# Revit family: MH-205-G
name_source: partatom
category: Plumbing Fixtures
revit_build: Autodesk Revit 2015 (Build: 20140322_1515(x64)
units: mm (PartAtom-declared; Revit-internal decimal feet)

## types (2) — shared parameters
A = 13"
A' = 6 1/2"
B = 11 25/32"
B' = 5 7/8"
B01 = 5 1/2"
C = 7 9/32"
C' = 3 21/32"
C'1 = 4 1/16"
Default Elevation = 48"
Manufacturer = MIFAB

MIFAB
MIFAB
PIPE SIZE = 2 15/16"
PIPE SIZE' = 1 15/32"
R1 = 7/32"
RP1 = 5/32"
RP2 = 3/16"
SC1 = 5/32"
SC2 = 1/8"
URL = www.mifab.com
V1 = No
V2 = No
V3 = No
V4 = No
V5 = Yes
V6 = No
id1 = 3/16"
id3 = 3/32"
linearL = 31/32"
linearW = 2 1/8"
od1 = 13/32"
od2 = 5/16"
od3 = 3/16"
r2 = 23/32"

## per-type parameters (varying)
| type | Connector Dia | D | Description | EE | EE1 | EE2 | EE3 | FF | G1 | G2 | HH1 | HH2 | II1 | II2 | ff2 |
| MH-305-G | 2 1/2" | 3 1/8" | 3" HydroMax Siphonic Gutter Drain | 3 3/4" | 2 29/32" | 3 9/32" | 29/32" | 0" | 3" | 5/32" | 2 1/2" | 1/4" | 5/32" | 3/16" | 3" |
| MH-205-G | 0" | 3 7/32" | 2" HydroMax Siphonic Gutter Drain | 2 7/16" | 2 7/32" | 2 3/8" | 7/8" | 11/32" | 1 31/32" | 1/8" | 1 3/4" | 1/8" | 3/32" | 3/32" | 2" |

note: column(s) folded — value = type name in every type: Model

## geometry (parser evidence)
native form markers: Sweep x2
no freeform markers — native parametric forms only
